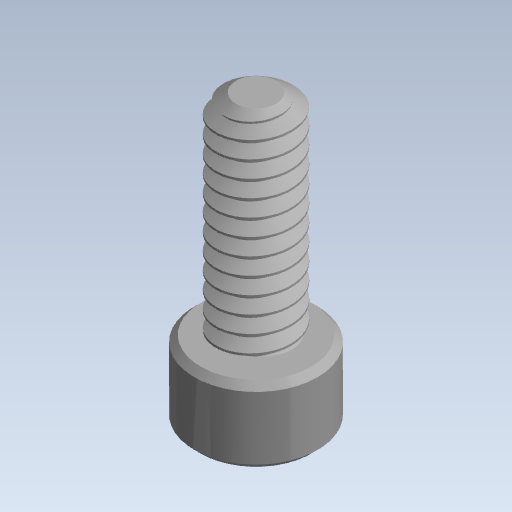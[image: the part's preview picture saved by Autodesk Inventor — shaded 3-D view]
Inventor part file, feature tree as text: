
AUTODESK INVENTOR PART (.ipt)
format: ipt  version: 2020 (Build 240168000, 168)  size: 494,592 bytes
history: native  units: mm (DEFAULTED — no unit token found)
features: chamfer x1
ambient origin geometry x8: Origin, YZ Plane, XZ Plane, XY Plane, X Axis, Y Axis, Z Axis, Center Point
bodies: Solid1 (feature_tree)
feature tree (1):
  chamfer  "Chamfer1"  [1 undecoded]
note: 1 required parameter value undecoded (feature->parameter linkage not recoverable at this tier; creation-order binding heuristic only, values carry confidence <= 0.55)
